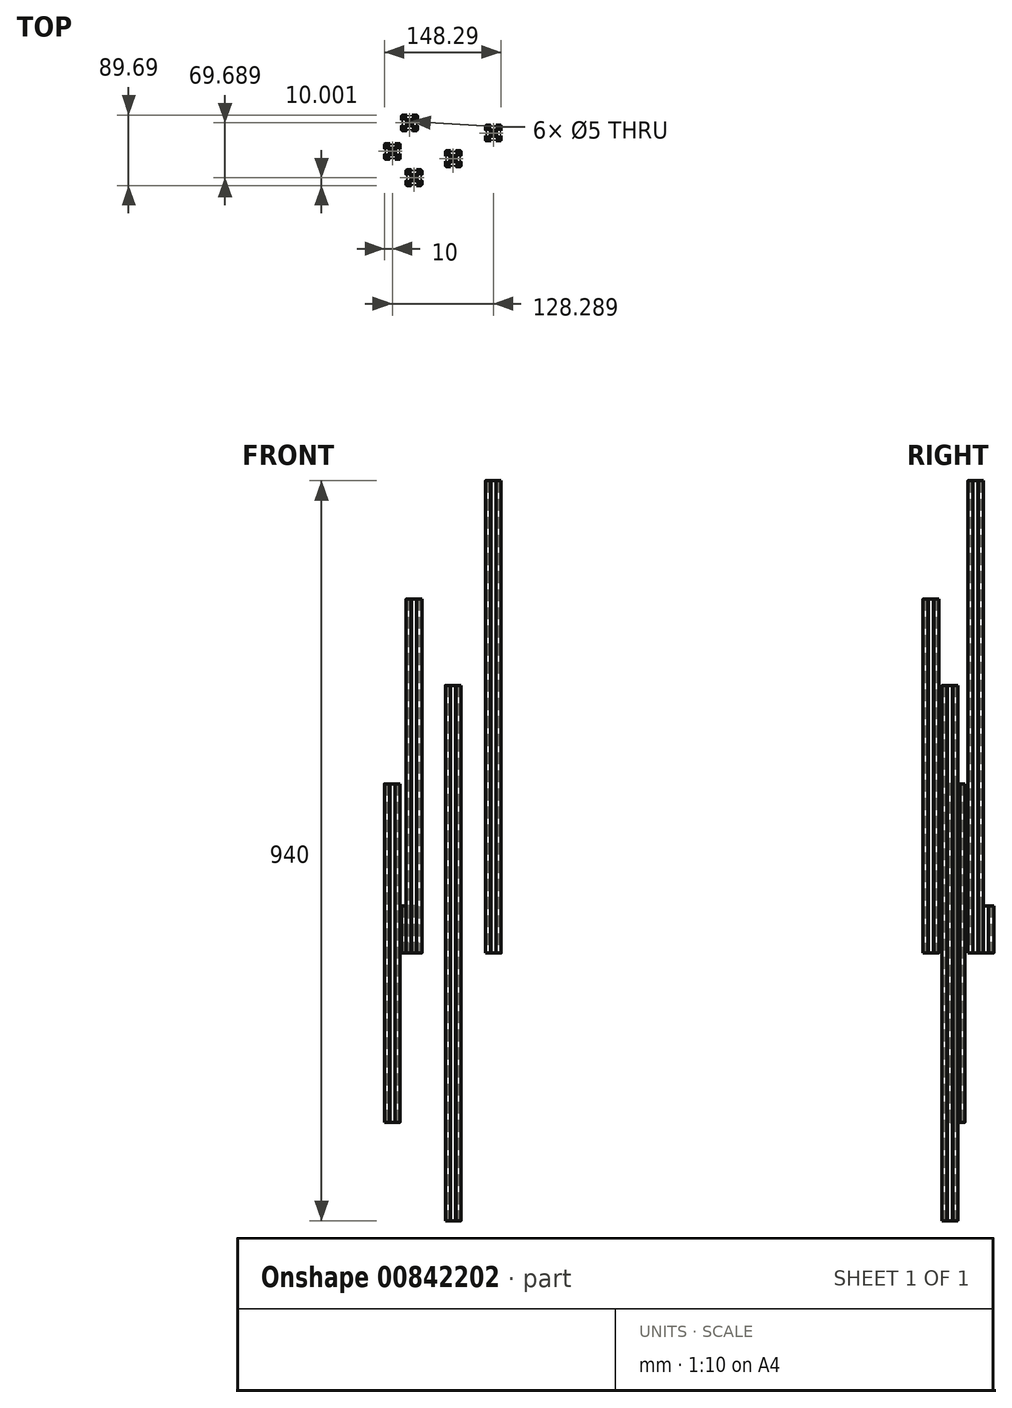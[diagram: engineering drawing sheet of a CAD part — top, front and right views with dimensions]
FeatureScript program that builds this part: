
annotation { "Feature Type Name" : "Feature", "Feature Type Description" : "" }
export const myFeature = defineFeature(function(context is Context, id is Id, definition is map)
    precondition{}
    {
        {
            var Q0;
            Q0=qCreatedBy(makeId("Top.planeOp"),FACE);
            var sketch = newSketch(context, id + "F0", { "sketchPlane" : qUnion([Q0])});
            skCircle(sketch, "E0", {"center": v(-10.22, 3.28) * mm, "radius": 2.5 * mm});
            skLineSegment(sketch, "E1.bottom", {"start": v(-1.72, -6.72) * mm, "end": v(-6.12, -6.72) * mm});
            skLineSegment(sketch, "E1.top", {"start": v(-1.72, 13.28) * mm, "end": v(-6.12, 13.28) * mm});
            skLineSegment(sketch, "E1.left", {"start": v(-0.22, -5.22) * mm, "end": v(-0.22, -0.32) * mm});
            skLineSegment(sketch, "E2.bottom", {"start": v(-8.21, -0.62) * mm, "end": v(-12.24, -0.62) * mm});
            skLineSegment(sketch, "E2.top", {"start": v(-8.21, 7.18) * mm, "end": v(-12.24, 7.18) * mm});
            skLineSegment(sketch, "E2.left", {"start": v(-6.32, 1.27) * mm, "end": v(-6.32, 5.3) * mm});
            skLineSegment(sketch, "E2.right", {"start": v(-14.12, 1.27) * mm, "end": v(-14.12, 5.3) * mm});
            skLineSegment(sketch, "E3.bottom", {"start": v(-1.72, 13.28) * mm, "end": v(-4.72, 13.28) * mm});
            skLineSegment(sketch, "E3.left", {"start": v(-0.22, 11.78) * mm, "end": v(-0.22, 8.78) * mm});
            skLineSegment(sketch, "E3.right", {"start": v(-4.72, 11.48) * mm, "end": v(-4.72, 9.84) * mm});
            skLineSegment(sketch, "E4", {"start": v(-5.74, 6.7) * mm, "end": v(-3.66, 8.78) * mm});
            skLineSegment(sketch, "E5.MirrorCS", {"start": v(-6.8, 7.77) * mm, "end": v(-4.72, 9.84) * mm});
            skLineSegment(sketch, "E6", {"start": v(-2.02, 8.78) * mm, "end": v(-2.02, 6.38) * mm});
            skLineSegment(sketch, "E7", {"start": v(-0.52, 6.88) * mm, "end": v(-0.22, 6.88) * mm});
            skLineSegment(sketch, "E8", {"start": v(-2.02, 6.38) * mm, "end": v(-0.72, 6.38) * mm});
            skLineSegment(sketch, "E9", {"start": v(-0.72, 6.68) * mm, "end": v(-0.72, 6.38) * mm});
            skPoint(sketch, "E10.visualSharp", {"position": v(-0.72, 6.88) * mm});
            skArc(sketch, "E10.filletArc", {"start": v(-0.52, 6.88) * mm, "mid": v(-0.67, 6.82) * mm, "end": v(-0.72, 6.68) * mm});
            skPoint(sketch, "E11.newPointA", {"position": v(-6.32, 6.12) * mm});
            skArc(sketch, "E11.filletArc", {"start": v(-5.74, 6.7) * mm, "mid": v(-6.17, 6.06) * mm, "end": v(-6.32, 5.3) * mm});
            skPoint(sketch, "E12.newPointA", {"position": v(-7.39, 7.18) * mm});
            skPoint(sketch, "E12.newPointB", {"position": v(-6.32, 7.18) * mm});
            skArc(sketch, "E12.filletArc", {"start": v(-8.21, 7.18) * mm, "mid": v(-7.45, 7.33) * mm, "end": v(-6.8, 7.77) * mm});
            skLineSegment(sketch, "E13.MirrorCS", {"start": v(-4.72, 11.48) * mm, "end": v(-7.12, 11.48) * mm});
            skLineSegment(sketch, "E14.MirrorCS", {"start": v(-7.12, 11.48) * mm, "end": v(-7.12, 12.78) * mm});
            skPoint(sketch, "E15.visualSharp", {"position": v(-0.22, 13.28) * mm});
            skArc(sketch, "E15.filletArc", {"start": v(-0.22, 11.78) * mm, "mid": v(-0.66, 12.84) * mm, "end": v(-1.72, 13.28) * mm});
            skLineSegment(sketch, "E16.trimOffspring", {"start": v(-2.02, 8.78) * mm, "end": v(-3.66, 8.78) * mm});
            skLineSegment(sketch, "E17.MirrorCS", {"start": v(-0.52, -0.32) * mm, "end": v(-0.22, -0.32) * mm});
            skArc(sketch, "E18.MirrorCS", {"start": v(-0.52, -0.32) * mm, "mid": v(-0.67, -0.26) * mm, "end": v(-0.72, -0.12) * mm});
            skLineSegment(sketch, "E19.MirrorCS", {"start": v(-0.72, -0.12) * mm, "end": v(-0.72, 0.18) * mm});
            skArc(sketch, "E20.MirrorCS", {"start": v(-5.74, -0.14) * mm, "mid": v(-6.17, 0.5) * mm, "end": v(-6.32, 1.27) * mm});
            skLineSegment(sketch, "E21.MirrorCS", {"start": v(-2.02, -2.22) * mm, "end": v(-3.66, -2.22) * mm});
            skLineSegment(sketch, "E22.MirrorCS", {"start": v(-2.02, 0.18) * mm, "end": v(-0.72, 0.18) * mm});
            skLineSegment(sketch, "E23.MirrorCS", {"start": v(-1.72, -6.72) * mm, "end": v(-4.72, -6.72) * mm});
            skPoint(sketch, "E24.MirrorP", {"position": v(-0.72, -0.32) * mm});
            skLineSegment(sketch, "E25.MirrorCS", {"start": v(-7.12, -4.92) * mm, "end": v(-7.12, -6.22) * mm});
            skLineSegment(sketch, "E26.MirrorCS", {"start": v(-4.72, -4.92) * mm, "end": v(-7.12, -4.92) * mm});
            skLineSegment(sketch, "E27.MirrorCS", {"start": v(-2.02, -2.22) * mm, "end": v(-2.02, 0.18) * mm});
            skLineSegment(sketch, "E28.MirrorCS", {"start": v(-0.22, -5.22) * mm, "end": v(-0.22, -2.22) * mm});
            skLineSegment(sketch, "E29.MirrorCS", {"start": v(-5.74, -0.14) * mm, "end": v(-3.66, -2.22) * mm});
            skPoint(sketch, "E30.MirrorP", {"position": v(-6.32, 0.44) * mm});
            skPoint(sketch, "E31.MirrorP", {"position": v(-0.22, -6.72) * mm});
            skPoint(sketch, "E32.MirrorP", {"position": v(-6.32, -0.62) * mm});
            skLineSegment(sketch, "E33.MirrorCS", {"start": v(-6.8, -1.2) * mm, "end": v(-4.72, -3.28) * mm});
            skPoint(sketch, "E34.MirrorP", {"position": v(-7.39, -0.62) * mm});
            skArc(sketch, "E35.MirrorCS", {"start": v(-0.22, -5.22) * mm, "mid": v(-0.66, -6.28) * mm, "end": v(-1.72, -6.72) * mm});
            skLineSegment(sketch, "E36.MirrorCS", {"start": v(-4.72, -4.92) * mm, "end": v(-4.72, -3.28) * mm});
            skArc(sketch, "E37.MirrorCS", {"start": v(-8.21, -0.62) * mm, "mid": v(-7.45, -0.77) * mm, "end": v(-6.8, -1.2) * mm});
            skLineSegment(sketch, "E38.trimOffspring", {"start": v(-0.22, 6.88) * mm, "end": v(-0.22, 11.78) * mm});
            skLineSegment(sketch, "E39.MirrorCS", {"start": v(-6.62, 12.98) * mm, "end": v(-6.62, 13.28) * mm});
            skArc(sketch, "E40.MirrorCS", {"start": v(-6.62, 12.98) * mm, "mid": v(-6.68, 12.84) * mm, "end": v(-6.82, 12.78) * mm});
            skLineSegment(sketch, "E41.MirrorCS", {"start": v(-6.82, 12.78) * mm, "end": v(-7.12, 12.78) * mm});
            skLineSegment(sketch, "E42", {"start": v(-6.12, 13.28) * mm, "end": v(-6.62, 13.28) * mm});
            skLineSegment(sketch, "E43.MirrorCS", {"start": v(-6.62, -6.42) * mm, "end": v(-6.62, -6.72) * mm});
            skLineSegment(sketch, "E44.MirrorCS", {"start": v(-6.82, -6.22) * mm, "end": v(-7.12, -6.22) * mm});
            skLineSegment(sketch, "E45.MirrorCS", {"start": v(-6.12, -6.72) * mm, "end": v(-6.62, -6.72) * mm});
            skArc(sketch, "E46.MirrorCS", {"start": v(-6.62, -6.42) * mm, "mid": v(-6.68, -6.28) * mm, "end": v(-6.82, -6.22) * mm});
            skArc(sketch, "E47.MirrorCS", {"start": v(-19.92, -0.32) * mm, "mid": v(-19.78, -0.26) * mm, "end": v(-19.72, -0.12) * mm});
            skLineSegment(sketch, "E48.MirrorCS", {"start": v(-19.92, 6.88) * mm, "end": v(-20.22, 6.88) * mm});
            skLineSegment(sketch, "E49.MirrorCS", {"start": v(-19.72, -0.12) * mm, "end": v(-19.72, 0.18) * mm});
            skArc(sketch, "E50.MirrorCS", {"start": v(-19.92, 6.88) * mm, "mid": v(-19.78, 6.82) * mm, "end": v(-19.72, 6.68) * mm});
            skLineSegment(sketch, "E51.MirrorCS", {"start": v(-19.72, 6.68) * mm, "end": v(-19.72, 6.38) * mm});
            skLineSegment(sketch, "E52.MirrorCS", {"start": v(-19.92, -0.32) * mm, "end": v(-20.22, -0.32) * mm});
            skLineSegment(sketch, "E53.MirrorCS", {"start": v(-14.32, 13.28) * mm, "end": v(-13.82, 13.28) * mm});
            skArc(sketch, "E54.MirrorCS", {"start": v(-20.22, -5.22) * mm, "mid": v(-19.79, -6.28) * mm, "end": v(-18.72, -6.72) * mm});
            skLineSegment(sketch, "E55.MirrorCS", {"start": v(-13.82, 12.98) * mm, "end": v(-13.82, 13.28) * mm});
            skArc(sketch, "E56.MirrorCS", {"start": v(-14.71, 6.7) * mm, "mid": v(-14.28, 6.06) * mm, "end": v(-14.12, 5.3) * mm});
            skLineSegment(sketch, "E57.MirrorCS", {"start": v(-13.62, -6.22) * mm, "end": v(-13.32, -6.22) * mm});
            skLineSegment(sketch, "E58.MirrorCS", {"start": v(-13.32, 11.48) * mm, "end": v(-13.32, 12.78) * mm});
            skLineSegment(sketch, "E59.MirrorCS", {"start": v(-12.24, 7.18) * mm, "end": v(-8.21, 7.18) * mm});
            skLineSegment(sketch, "E60.MirrorCS", {"start": v(-18.42, 0.18) * mm, "end": v(-19.72, 0.18) * mm});
            skLineSegment(sketch, "E61.MirrorCS", {"start": v(-18.42, 6.38) * mm, "end": v(-19.72, 6.38) * mm});
            skLineSegment(sketch, "E62.MirrorCS", {"start": v(-13.62, 12.78) * mm, "end": v(-13.32, 12.78) * mm});
            skArc(sketch, "E63.MirrorCS", {"start": v(-14.71, -0.14) * mm, "mid": v(-14.28, 0.5) * mm, "end": v(-14.12, 1.27) * mm});
            skArc(sketch, "E64.MirrorCS", {"start": v(-13.82, -6.42) * mm, "mid": v(-13.77, -6.28) * mm, "end": v(-13.62, -6.22) * mm});
            skArc(sketch, "E65.MirrorCS", {"start": v(-13.82, 12.98) * mm, "mid": v(-13.77, 12.84) * mm, "end": v(-13.62, 12.78) * mm});
            skLineSegment(sketch, "E66.MirrorCS", {"start": v(-13.82, -6.42) * mm, "end": v(-13.82, -6.72) * mm});
            skLineSegment(sketch, "E67.MirrorCS", {"start": v(-12.24, -0.62) * mm, "end": v(-8.21, -0.62) * mm});
            skLineSegment(sketch, "E68.MirrorCS", {"start": v(-14.32, -6.72) * mm, "end": v(-13.82, -6.72) * mm});
            skLineSegment(sketch, "E69.MirrorCS", {"start": v(-13.32, -4.92) * mm, "end": v(-13.32, -6.22) * mm});
            skArc(sketch, "E70.MirrorCS", {"start": v(-12.24, 7.18) * mm, "mid": v(-13, 7.33) * mm, "end": v(-13.65, 7.77) * mm});
            skPoint(sketch, "E71.MirrorP", {"position": v(-20.22, -6.72) * mm});
            skLineSegment(sketch, "E72.MirrorCS", {"start": v(-18.72, -6.72) * mm, "end": v(-14.32, -6.72) * mm});
            skPoint(sketch, "E73.MirrorP", {"position": v(-14.12, -0.62) * mm});
            skLineSegment(sketch, "E74.MirrorCS", {"start": v(-18.72, 13.28) * mm, "end": v(-14.32, 13.28) * mm});
            skArc(sketch, "E75.MirrorCS", {"start": v(-12.24, -0.62) * mm, "mid": v(-13, -0.77) * mm, "end": v(-13.65, -1.2) * mm});
            skArc(sketch, "E76.MirrorCS", {"start": v(-20.22, 11.78) * mm, "mid": v(-19.79, 12.84) * mm, "end": v(-18.72, 13.28) * mm});
            skPoint(sketch, "E77.MirrorP", {"position": v(-14.12, 0.44) * mm});
            skLineSegment(sketch, "E78.MirrorCS", {"start": v(-15.72, 11.48) * mm, "end": v(-15.72, 9.84) * mm});
            skLineSegment(sketch, "E79.MirrorCS", {"start": v(-13.65, 7.77) * mm, "end": v(-15.72, 9.84) * mm});
            skPoint(sketch, "E80.MirrorP", {"position": v(-14.12, 6.12) * mm});
            skLineSegment(sketch, "E81.MirrorCS", {"start": v(-18.42, -2.22) * mm, "end": v(-18.42, 0.18) * mm});
            skLineSegment(sketch, "E82.MirrorCS", {"start": v(-14.71, -0.14) * mm, "end": v(-16.79, -2.22) * mm});
            skLineSegment(sketch, "E83.MirrorCS", {"start": v(-15.72, -4.92) * mm, "end": v(-13.32, -4.92) * mm});
            skLineSegment(sketch, "E84.MirrorCS", {"start": v(-18.42, -2.22) * mm, "end": v(-16.79, -2.22) * mm});
            skLineSegment(sketch, "E85.MirrorCS", {"start": v(-20.22, -5.22) * mm, "end": v(-20.22, -2.22) * mm});
            skLineSegment(sketch, "E86.MirrorCS", {"start": v(-18.72, 13.28) * mm, "end": v(-15.72, 13.28) * mm});
            skLineSegment(sketch, "E87.MirrorCS", {"start": v(-20.22, 6.88) * mm, "end": v(-20.22, 11.78) * mm});
            skLineSegment(sketch, "E88.MirrorCS", {"start": v(-15.72, 11.48) * mm, "end": v(-13.32, 11.48) * mm});
            skLineSegment(sketch, "E89.MirrorCS", {"start": v(-13.65, -1.2) * mm, "end": v(-15.72, -3.28) * mm});
            skPoint(sketch, "E90.MirrorP", {"position": v(-13.06, -0.62) * mm});
            skLineSegment(sketch, "E91.MirrorCS", {"start": v(-18.42, 8.78) * mm, "end": v(-18.42, 6.38) * mm});
            skLineSegment(sketch, "E92.MirrorCS", {"start": v(-20.22, 11.78) * mm, "end": v(-20.22, 8.78) * mm});
            skPoint(sketch, "E93.MirrorP", {"position": v(-19.72, -0.32) * mm});
            skPoint(sketch, "E94.MirrorP", {"position": v(-20.22, 13.28) * mm});
            skPoint(sketch, "E95.MirrorP", {"position": v(-19.72, 6.88) * mm});
            skLineSegment(sketch, "E96.MirrorCS", {"start": v(-14.71, 6.7) * mm, "end": v(-16.79, 8.78) * mm});
            skLineSegment(sketch, "E97.MirrorCS", {"start": v(-18.42, 8.78) * mm, "end": v(-16.79, 8.78) * mm});
            skLineSegment(sketch, "E98.MirrorCS", {"start": v(-20.22, -5.22) * mm, "end": v(-20.22, -0.32) * mm});
            skLineSegment(sketch, "E99.MirrorCS", {"start": v(-18.72, -6.72) * mm, "end": v(-15.72, -6.72) * mm});
            skPoint(sketch, "E100.MirrorP", {"position": v(-14.12, 7.18) * mm});
            skPoint(sketch, "E101.MirrorP", {"position": v(-13.06, 7.18) * mm});
            skLineSegment(sketch, "E102.MirrorCS", {"start": v(-15.72, -4.92) * mm, "end": v(-15.72, -3.28) * mm});
            skSolve(sketch);
        }
        {
            var Q0;
            Q0=makeQuery(id+"F0.imprint","IMPRINT",FACE,{"disambiguationData":[TD([[makeQuery(id+"F0.imprint","IMPRINT",EDGE,{"derivedFrom":sQuery(id+"F0.wireOp",EDGE,"E1.bottom")}),-1.0]])]});
            extrude(context, id + "F1", {"entities" : qUnion([Q0]), "endBound" : BoundingType.SYMMETRIC, "depth" : 680 * mm, "offsetDistance" : 25 * mm});
        }
        {
            var Q0;
            Q0=qCreatedBy(makeId("Top.planeOp"),FACE);
            var sketch = newSketch(context, id + "F2", { "sketchPlane" : qUnion([Q0])});
            skCircle(sketch, "E103", {"center": v(-87.46, 12.57) * mm, "radius": 2.5 * mm});
            skLineSegment(sketch, "E104.bottom", {"start": v(-78.96, 2.57) * mm, "end": v(-83.36, 2.57) * mm});
            skLineSegment(sketch, "E104.top", {"start": v(-78.96, 22.57) * mm, "end": v(-83.36, 22.57) * mm});
            skLineSegment(sketch, "E104.left", {"start": v(-77.46, 4.07) * mm, "end": v(-77.46, 8.97) * mm});
            skLineSegment(sketch, "E105.bottom", {"start": v(-85.45, 8.67) * mm, "end": v(-89.47, 8.67) * mm});
            skLineSegment(sketch, "E105.top", {"start": v(-85.45, 16.47) * mm, "end": v(-89.47, 16.47) * mm});
            skLineSegment(sketch, "E105.left", {"start": v(-83.56, 10.56) * mm, "end": v(-83.56, 14.58) * mm});
            skLineSegment(sketch, "E105.right", {"start": v(-91.36, 10.56) * mm, "end": v(-91.36, 14.58) * mm});
            skLineSegment(sketch, "E106.bottom", {"start": v(-78.96, 22.57) * mm, "end": v(-81.96, 22.57) * mm});
            skLineSegment(sketch, "E106.left", {"start": v(-77.46, 21.07) * mm, "end": v(-77.46, 18.07) * mm});
            skLineSegment(sketch, "E106.right", {"start": v(-81.96, 20.77) * mm, "end": v(-81.96, 19.13) * mm});
            skLineSegment(sketch, "E107", {"start": v(-82.97, 16) * mm, "end": v(-80.9, 18.07) * mm});
            skLineSegment(sketch, "E108.MirrorCS", {"start": v(-84.04, 17.06) * mm, "end": v(-81.96, 19.13) * mm});
            skLineSegment(sketch, "E109", {"start": v(-79.26, 18.07) * mm, "end": v(-79.26, 15.67) * mm});
            skLineSegment(sketch, "E110", {"start": v(-77.76, 16.17) * mm, "end": v(-77.46, 16.17) * mm});
            skLineSegment(sketch, "E111", {"start": v(-79.26, 15.67) * mm, "end": v(-77.96, 15.67) * mm});
            skLineSegment(sketch, "E112", {"start": v(-77.96, 15.97) * mm, "end": v(-77.96, 15.67) * mm});
            skPoint(sketch, "E113.visualSharp", {"position": v(-77.96, 16.17) * mm});
            skArc(sketch, "E113.filletArc", {"start": v(-77.76, 16.17) * mm, "mid": v(-77.9, 16.11) * mm, "end": v(-77.96, 15.97) * mm});
            skPoint(sketch, "E114.newPointA", {"position": v(-83.56, 15.4) * mm});
            skArc(sketch, "E114.filletArc", {"start": v(-82.97, 16) * mm, "mid": v(-83.4, 15.35) * mm, "end": v(-83.56, 14.58) * mm});
            skPoint(sketch, "E115.newPointA", {"position": v(-84.62, 16.47) * mm});
            skPoint(sketch, "E115.newPointB", {"position": v(-83.56, 16.47) * mm});
            skArc(sketch, "E115.filletArc", {"start": v(-85.45, 16.47) * mm, "mid": v(-84.68, 16.62) * mm, "end": v(-84.04, 17.06) * mm});
            skLineSegment(sketch, "E116.MirrorCS", {"start": v(-81.96, 20.77) * mm, "end": v(-84.36, 20.77) * mm});
            skLineSegment(sketch, "E117.MirrorCS", {"start": v(-84.36, 20.77) * mm, "end": v(-84.36, 22.07) * mm});
            skPoint(sketch, "E118.visualSharp", {"position": v(-77.46, 22.57) * mm});
            skArc(sketch, "E118.filletArc", {"start": v(-77.46, 21.07) * mm, "mid": v(-77.9, 22.13) * mm, "end": v(-78.96, 22.57) * mm});
            skLineSegment(sketch, "E119.trimOffspring", {"start": v(-79.26, 18.07) * mm, "end": v(-80.9, 18.07) * mm});
            skLineSegment(sketch, "E120.MirrorCS", {"start": v(-77.76, 8.97) * mm, "end": v(-77.46, 8.97) * mm});
            skArc(sketch, "E121.MirrorCS", {"start": v(-77.76, 8.97) * mm, "mid": v(-77.9, 9.03) * mm, "end": v(-77.96, 9.17) * mm});
            skLineSegment(sketch, "E122.MirrorCS", {"start": v(-77.96, 9.17) * mm, "end": v(-77.96, 9.47) * mm});
            skArc(sketch, "E123.MirrorCS", {"start": v(-82.97, 9.15) * mm, "mid": v(-83.4, 9.8) * mm, "end": v(-83.56, 10.56) * mm});
            skLineSegment(sketch, "E124.MirrorCS", {"start": v(-79.26, 7.07) * mm, "end": v(-80.9, 7.07) * mm});
            skLineSegment(sketch, "E125.MirrorCS", {"start": v(-79.26, 9.47) * mm, "end": v(-77.96, 9.47) * mm});
            skLineSegment(sketch, "E126.MirrorCS", {"start": v(-78.96, 2.57) * mm, "end": v(-81.96, 2.57) * mm});
            skPoint(sketch, "E127.MirrorP", {"position": v(-77.96, 8.97) * mm});
            skLineSegment(sketch, "E128.MirrorCS", {"start": v(-84.36, 4.37) * mm, "end": v(-84.36, 3.07) * mm});
            skLineSegment(sketch, "E129.MirrorCS", {"start": v(-81.96, 4.37) * mm, "end": v(-84.36, 4.37) * mm});
            skLineSegment(sketch, "E130.MirrorCS", {"start": v(-79.26, 7.07) * mm, "end": v(-79.26, 9.47) * mm});
            skLineSegment(sketch, "E131.MirrorCS", {"start": v(-77.46, 4.07) * mm, "end": v(-77.46, 7.07) * mm});
            skLineSegment(sketch, "E132.MirrorCS", {"start": v(-82.97, 9.15) * mm, "end": v(-80.9, 7.07) * mm});
            skPoint(sketch, "E133.MirrorP", {"position": v(-83.56, 9.73) * mm});
            skPoint(sketch, "E134.MirrorP", {"position": v(-77.46, 2.57) * mm});
            skPoint(sketch, "E135.MirrorP", {"position": v(-83.56, 8.67) * mm});
            skLineSegment(sketch, "E136.MirrorCS", {"start": v(-84.04, 8.08) * mm, "end": v(-81.96, 6) * mm});
            skPoint(sketch, "E137.MirrorP", {"position": v(-84.62, 8.67) * mm});
            skArc(sketch, "E138.MirrorCS", {"start": v(-77.46, 4.07) * mm, "mid": v(-77.9, 3) * mm, "end": v(-78.96, 2.57) * mm});
            skLineSegment(sketch, "E139.MirrorCS", {"start": v(-81.96, 4.37) * mm, "end": v(-81.96, 6) * mm});
            skArc(sketch, "E140.MirrorCS", {"start": v(-85.45, 8.67) * mm, "mid": v(-84.68, 8.52) * mm, "end": v(-84.04, 8.08) * mm});
            skLineSegment(sketch, "E141.trimOffspring", {"start": v(-77.46, 16.17) * mm, "end": v(-77.46, 21.07) * mm});
            skLineSegment(sketch, "E142.MirrorCS", {"start": v(-83.86, 22.27) * mm, "end": v(-83.86, 22.57) * mm});
            skArc(sketch, "E143.MirrorCS", {"start": v(-83.86, 22.27) * mm, "mid": v(-83.92, 22.13) * mm, "end": v(-84.06, 22.07) * mm});
            skLineSegment(sketch, "E144.MirrorCS", {"start": v(-84.06, 22.07) * mm, "end": v(-84.36, 22.07) * mm});
            skLineSegment(sketch, "E145", {"start": v(-83.36, 22.57) * mm, "end": v(-83.86, 22.57) * mm});
            skLineSegment(sketch, "E146.MirrorCS", {"start": v(-83.86, 2.87) * mm, "end": v(-83.86, 2.57) * mm});
            skLineSegment(sketch, "E147.MirrorCS", {"start": v(-84.06, 3.07) * mm, "end": v(-84.36, 3.07) * mm});
            skLineSegment(sketch, "E148.MirrorCS", {"start": v(-83.36, 2.57) * mm, "end": v(-83.86, 2.57) * mm});
            skArc(sketch, "E149.MirrorCS", {"start": v(-83.86, 2.87) * mm, "mid": v(-83.92, 3.01) * mm, "end": v(-84.06, 3.07) * mm});
            skArc(sketch, "E150.MirrorCS", {"start": v(-97.16, 8.97) * mm, "mid": v(-97.02, 9.03) * mm, "end": v(-96.96, 9.17) * mm});
            skLineSegment(sketch, "E151.MirrorCS", {"start": v(-97.16, 16.17) * mm, "end": v(-97.46, 16.17) * mm});
            skLineSegment(sketch, "E152.MirrorCS", {"start": v(-96.96, 9.17) * mm, "end": v(-96.96, 9.47) * mm});
            skArc(sketch, "E153.MirrorCS", {"start": v(-97.16, 16.17) * mm, "mid": v(-97.02, 16.11) * mm, "end": v(-96.96, 15.97) * mm});
            skLineSegment(sketch, "E154.MirrorCS", {"start": v(-96.96, 15.97) * mm, "end": v(-96.96, 15.67) * mm});
            skLineSegment(sketch, "E155.MirrorCS", {"start": v(-97.16, 8.97) * mm, "end": v(-97.46, 8.97) * mm});
            skLineSegment(sketch, "E156.MirrorCS", {"start": v(-91.56, 22.57) * mm, "end": v(-91.06, 22.57) * mm});
            skArc(sketch, "E157.MirrorCS", {"start": v(-97.46, 4.07) * mm, "mid": v(-97.02, 3) * mm, "end": v(-95.96, 2.57) * mm});
            skLineSegment(sketch, "E158.MirrorCS", {"start": v(-91.06, 22.27) * mm, "end": v(-91.06, 22.57) * mm});
            skArc(sketch, "E159.MirrorCS", {"start": v(-91.95, 16) * mm, "mid": v(-91.51, 15.35) * mm, "end": v(-91.36, 14.58) * mm});
            skLineSegment(sketch, "E160.MirrorCS", {"start": v(-90.86, 3.07) * mm, "end": v(-90.56, 3.07) * mm});
            skLineSegment(sketch, "E161.MirrorCS", {"start": v(-90.56, 20.77) * mm, "end": v(-90.56, 22.07) * mm});
            skLineSegment(sketch, "E162.MirrorCS", {"start": v(-89.47, 16.47) * mm, "end": v(-85.45, 16.47) * mm});
            skLineSegment(sketch, "E163.MirrorCS", {"start": v(-95.66, 9.47) * mm, "end": v(-96.96, 9.47) * mm});
            skLineSegment(sketch, "E164.MirrorCS", {"start": v(-95.66, 15.67) * mm, "end": v(-96.96, 15.67) * mm});
            skLineSegment(sketch, "E165.MirrorCS", {"start": v(-90.86, 22.07) * mm, "end": v(-90.56, 22.07) * mm});
            skArc(sketch, "E166.MirrorCS", {"start": v(-91.95, 9.15) * mm, "mid": v(-91.51, 9.8) * mm, "end": v(-91.36, 10.56) * mm});
            skArc(sketch, "E167.MirrorCS", {"start": v(-91.06, 2.87) * mm, "mid": v(-91, 3.01) * mm, "end": v(-90.86, 3.07) * mm});
            skArc(sketch, "E168.MirrorCS", {"start": v(-91.06, 22.27) * mm, "mid": v(-91, 22.13) * mm, "end": v(-90.86, 22.07) * mm});
            skLineSegment(sketch, "E169.MirrorCS", {"start": v(-91.06, 2.87) * mm, "end": v(-91.06, 2.57) * mm});
            skLineSegment(sketch, "E170.MirrorCS", {"start": v(-89.47, 8.67) * mm, "end": v(-85.45, 8.67) * mm});
            skLineSegment(sketch, "E171.MirrorCS", {"start": v(-91.56, 2.57) * mm, "end": v(-91.06, 2.57) * mm});
            skLineSegment(sketch, "E172.MirrorCS", {"start": v(-90.56, 4.37) * mm, "end": v(-90.56, 3.07) * mm});
            skArc(sketch, "E173.MirrorCS", {"start": v(-89.47, 16.47) * mm, "mid": v(-90.24, 16.62) * mm, "end": v(-90.89, 17.06) * mm});
            skPoint(sketch, "E174.MirrorP", {"position": v(-97.46, 2.57) * mm});
            skLineSegment(sketch, "E175.MirrorCS", {"start": v(-95.96, 2.57) * mm, "end": v(-91.56, 2.57) * mm});
            skPoint(sketch, "E176.MirrorP", {"position": v(-91.36, 8.67) * mm});
            skLineSegment(sketch, "E177.MirrorCS", {"start": v(-95.96, 22.57) * mm, "end": v(-91.56, 22.57) * mm});
            skArc(sketch, "E178.MirrorCS", {"start": v(-89.47, 8.67) * mm, "mid": v(-90.24, 8.52) * mm, "end": v(-90.89, 8.08) * mm});
            skArc(sketch, "E179.MirrorCS", {"start": v(-97.46, 21.07) * mm, "mid": v(-97.02, 22.13) * mm, "end": v(-95.96, 22.57) * mm});
            skPoint(sketch, "E180.MirrorP", {"position": v(-91.36, 9.73) * mm});
            skLineSegment(sketch, "E181.MirrorCS", {"start": v(-92.96, 20.77) * mm, "end": v(-92.96, 19.13) * mm});
            skLineSegment(sketch, "E182.MirrorCS", {"start": v(-90.89, 17.06) * mm, "end": v(-92.96, 19.13) * mm});
            skPoint(sketch, "E183.MirrorP", {"position": v(-91.36, 15.4) * mm});
            skLineSegment(sketch, "E184.MirrorCS", {"start": v(-95.66, 7.07) * mm, "end": v(-95.66, 9.47) * mm});
            skLineSegment(sketch, "E185.MirrorCS", {"start": v(-91.95, 9.15) * mm, "end": v(-94.02, 7.07) * mm});
            skLineSegment(sketch, "E186.MirrorCS", {"start": v(-92.96, 4.37) * mm, "end": v(-90.56, 4.37) * mm});
            skLineSegment(sketch, "E187.MirrorCS", {"start": v(-95.66, 7.07) * mm, "end": v(-94.02, 7.07) * mm});
            skLineSegment(sketch, "E188.MirrorCS", {"start": v(-97.46, 4.07) * mm, "end": v(-97.46, 7.07) * mm});
            skLineSegment(sketch, "E189.MirrorCS", {"start": v(-95.96, 22.57) * mm, "end": v(-92.96, 22.57) * mm});
            skLineSegment(sketch, "E190.MirrorCS", {"start": v(-97.46, 16.17) * mm, "end": v(-97.46, 21.07) * mm});
            skLineSegment(sketch, "E191.MirrorCS", {"start": v(-92.96, 20.77) * mm, "end": v(-90.56, 20.77) * mm});
            skLineSegment(sketch, "E192.MirrorCS", {"start": v(-90.89, 8.08) * mm, "end": v(-92.96, 6) * mm});
            skPoint(sketch, "E193.MirrorP", {"position": v(-90.3, 8.67) * mm});
            skLineSegment(sketch, "E194.MirrorCS", {"start": v(-95.66, 18.07) * mm, "end": v(-95.66, 15.67) * mm});
            skLineSegment(sketch, "E195.MirrorCS", {"start": v(-97.46, 21.07) * mm, "end": v(-97.46, 18.07) * mm});
            skPoint(sketch, "E196.MirrorP", {"position": v(-96.96, 8.97) * mm});
            skPoint(sketch, "E197.MirrorP", {"position": v(-97.46, 22.57) * mm});
            skPoint(sketch, "E198.MirrorP", {"position": v(-96.96, 16.17) * mm});
            skLineSegment(sketch, "E199.MirrorCS", {"start": v(-91.95, 16) * mm, "end": v(-94.02, 18.07) * mm});
            skLineSegment(sketch, "E200.MirrorCS", {"start": v(-95.66, 18.07) * mm, "end": v(-94.02, 18.07) * mm});
            skLineSegment(sketch, "E201.MirrorCS", {"start": v(-97.46, 4.07) * mm, "end": v(-97.46, 8.97) * mm});
            skLineSegment(sketch, "E202.MirrorCS", {"start": v(-95.96, 2.57) * mm, "end": v(-92.96, 2.57) * mm});
            skPoint(sketch, "E203.MirrorP", {"position": v(-91.36, 16.47) * mm});
            skPoint(sketch, "E204.MirrorP", {"position": v(-90.3, 16.47) * mm});
            skLineSegment(sketch, "E205.MirrorCS", {"start": v(-92.96, 4.37) * mm, "end": v(-92.96, 6) * mm});
            skSolve(sketch);
        }
        {
            var Q0;
            Q0=makeQuery(id+"F2.imprint","IMPRINT",FACE,{"disambiguationData":[TD([[makeQuery(id+"F2.imprint","IMPRINT",EDGE,{"derivedFrom":sQuery(id+"F2.wireOp",EDGE,"E104.bottom")}),-1.0]])]});
            extrude(context, id + "F3", {"entities" : qUnion([Q0]), "endBound" : BoundingType.SYMMETRIC, "depth" : 430 * mm, "offsetDistance" : 25 * mm});
        }
        {
            var Q0;
            Q0=qCreatedBy(makeId("Top.planeOp"),FACE);
            var sketch = newSketch(context, id + "F4", { "sketchPlane" : qUnion([Q0])});
            skCircle(sketch, "E206", {"center": v(40.83, 35.88) * mm, "radius": 2.5 * mm});
            skLineSegment(sketch, "E207.bottom", {"start": v(49.33, 25.88) * mm, "end": v(44.93, 25.88) * mm});
            skLineSegment(sketch, "E207.top", {"start": v(49.33, 45.88) * mm, "end": v(44.93, 45.88) * mm});
            skLineSegment(sketch, "E207.left", {"start": v(50.83, 27.38) * mm, "end": v(50.83, 32.28) * mm});
            skLineSegment(sketch, "E208.bottom", {"start": v(42.84, 31.98) * mm, "end": v(38.82, 31.98) * mm});
            skLineSegment(sketch, "E208.top", {"start": v(42.84, 39.78) * mm, "end": v(38.82, 39.78) * mm});
            skLineSegment(sketch, "E208.left", {"start": v(44.73, 33.87) * mm, "end": v(44.73, 37.9) * mm});
            skLineSegment(sketch, "E208.right", {"start": v(36.93, 33.87) * mm, "end": v(36.93, 37.9) * mm});
            skLineSegment(sketch, "E209.bottom", {"start": v(49.33, 45.88) * mm, "end": v(46.33, 45.88) * mm});
            skLineSegment(sketch, "E209.left", {"start": v(50.83, 44.38) * mm, "end": v(50.83, 41.38) * mm});
            skLineSegment(sketch, "E209.right", {"start": v(46.33, 44.08) * mm, "end": v(46.33, 42.45) * mm});
            skLineSegment(sketch, "E210", {"start": v(45.31, 39.31) * mm, "end": v(47.39, 41.38) * mm});
            skLineSegment(sketch, "E211.MirrorCS", {"start": v(44.25, 40.37) * mm, "end": v(46.33, 42.45) * mm});
            skLineSegment(sketch, "E212", {"start": v(49.03, 41.38) * mm, "end": v(49.03, 38.98) * mm});
            skLineSegment(sketch, "E213", {"start": v(50.53, 39.48) * mm, "end": v(50.83, 39.48) * mm});
            skLineSegment(sketch, "E214", {"start": v(49.03, 38.98) * mm, "end": v(50.33, 38.98) * mm});
            skLineSegment(sketch, "E215", {"start": v(50.33, 39.28) * mm, "end": v(50.33, 38.98) * mm});
            skPoint(sketch, "E216.visualSharp", {"position": v(50.33, 39.48) * mm});
            skArc(sketch, "E216.filletArc", {"start": v(50.53, 39.48) * mm, "mid": v(50.39, 39.43) * mm, "end": v(50.33, 39.28) * mm});
            skPoint(sketch, "E217.newPointA", {"position": v(44.73, 38.72) * mm});
            skArc(sketch, "E217.filletArc", {"start": v(45.31, 39.31) * mm, "mid": v(44.88, 38.66) * mm, "end": v(44.73, 37.9) * mm});
            skPoint(sketch, "E218.newPointA", {"position": v(43.67, 39.78) * mm});
            skPoint(sketch, "E218.newPointB", {"position": v(44.73, 39.78) * mm});
            skArc(sketch, "E218.filletArc", {"start": v(42.84, 39.78) * mm, "mid": v(43.6, 39.94) * mm, "end": v(44.25, 40.37) * mm});
            skLineSegment(sketch, "E219.MirrorCS", {"start": v(46.33, 44.08) * mm, "end": v(43.93, 44.08) * mm});
            skLineSegment(sketch, "E220.MirrorCS", {"start": v(43.93, 44.08) * mm, "end": v(43.93, 45.38) * mm});
            skPoint(sketch, "E221.visualSharp", {"position": v(50.83, 45.88) * mm});
            skArc(sketch, "E221.filletArc", {"start": v(50.83, 44.38) * mm, "mid": v(50.39, 45.45) * mm, "end": v(49.33, 45.88) * mm});
            skLineSegment(sketch, "E222.trimOffspring", {"start": v(49.03, 41.38) * mm, "end": v(47.39, 41.38) * mm});
            skLineSegment(sketch, "E223.MirrorCS", {"start": v(50.53, 32.28) * mm, "end": v(50.83, 32.28) * mm});
            skArc(sketch, "E224.MirrorCS", {"start": v(50.53, 32.28) * mm, "mid": v(50.39, 32.34) * mm, "end": v(50.33, 32.48) * mm});
            skLineSegment(sketch, "E225.MirrorCS", {"start": v(50.33, 32.48) * mm, "end": v(50.33, 32.78) * mm});
            skArc(sketch, "E226.MirrorCS", {"start": v(45.31, 32.46) * mm, "mid": v(44.88, 33.1) * mm, "end": v(44.73, 33.87) * mm});
            skLineSegment(sketch, "E227.MirrorCS", {"start": v(49.03, 30.38) * mm, "end": v(47.39, 30.38) * mm});
            skLineSegment(sketch, "E228.MirrorCS", {"start": v(49.03, 32.78) * mm, "end": v(50.33, 32.78) * mm});
            skLineSegment(sketch, "E229.MirrorCS", {"start": v(49.33, 25.88) * mm, "end": v(46.33, 25.88) * mm});
            skPoint(sketch, "E230.MirrorP", {"position": v(50.33, 32.28) * mm});
            skLineSegment(sketch, "E231.MirrorCS", {"start": v(43.93, 27.68) * mm, "end": v(43.93, 26.38) * mm});
            skLineSegment(sketch, "E232.MirrorCS", {"start": v(46.33, 27.68) * mm, "end": v(43.93, 27.68) * mm});
            skLineSegment(sketch, "E233.MirrorCS", {"start": v(49.03, 30.38) * mm, "end": v(49.03, 32.78) * mm});
            skLineSegment(sketch, "E234.MirrorCS", {"start": v(50.83, 27.38) * mm, "end": v(50.83, 30.38) * mm});
            skLineSegment(sketch, "E235.MirrorCS", {"start": v(45.31, 32.46) * mm, "end": v(47.39, 30.38) * mm});
            skPoint(sketch, "E236.MirrorP", {"position": v(44.73, 33.05) * mm});
            skPoint(sketch, "E237.MirrorP", {"position": v(50.83, 25.88) * mm});
            skPoint(sketch, "E238.MirrorP", {"position": v(44.73, 31.98) * mm});
            skLineSegment(sketch, "E239.MirrorCS", {"start": v(44.25, 31.4) * mm, "end": v(46.33, 29.32) * mm});
            skPoint(sketch, "E240.MirrorP", {"position": v(43.67, 31.98) * mm});
            skArc(sketch, "E241.MirrorCS", {"start": v(50.83, 27.38) * mm, "mid": v(50.39, 26.32) * mm, "end": v(49.33, 25.88) * mm});
            skLineSegment(sketch, "E242.MirrorCS", {"start": v(46.33, 27.68) * mm, "end": v(46.33, 29.32) * mm});
            skArc(sketch, "E243.MirrorCS", {"start": v(42.84, 31.98) * mm, "mid": v(43.6, 31.83) * mm, "end": v(44.25, 31.4) * mm});
            skLineSegment(sketch, "E244.trimOffspring", {"start": v(50.83, 39.48) * mm, "end": v(50.83, 44.38) * mm});
            skLineSegment(sketch, "E245.MirrorCS", {"start": v(44.43, 45.58) * mm, "end": v(44.43, 45.88) * mm});
            skArc(sketch, "E246.MirrorCS", {"start": v(44.43, 45.58) * mm, "mid": v(44.37, 45.44) * mm, "end": v(44.23, 45.38) * mm});
            skLineSegment(sketch, "E247.MirrorCS", {"start": v(44.23, 45.38) * mm, "end": v(43.93, 45.38) * mm});
            skLineSegment(sketch, "E248", {"start": v(44.93, 45.88) * mm, "end": v(44.43, 45.88) * mm});
            skLineSegment(sketch, "E249.MirrorCS", {"start": v(44.43, 26.18) * mm, "end": v(44.43, 25.88) * mm});
            skLineSegment(sketch, "E250.MirrorCS", {"start": v(44.23, 26.38) * mm, "end": v(43.93, 26.38) * mm});
            skLineSegment(sketch, "E251.MirrorCS", {"start": v(44.93, 25.88) * mm, "end": v(44.43, 25.88) * mm});
            skArc(sketch, "E252.MirrorCS", {"start": v(44.43, 26.18) * mm, "mid": v(44.37, 26.33) * mm, "end": v(44.23, 26.38) * mm});
            skArc(sketch, "E253.MirrorCS", {"start": v(31.13, 32.28) * mm, "mid": v(31.27, 32.34) * mm, "end": v(31.33, 32.48) * mm});
            skLineSegment(sketch, "E254.MirrorCS", {"start": v(31.13, 39.48) * mm, "end": v(30.83, 39.48) * mm});
            skLineSegment(sketch, "E255.MirrorCS", {"start": v(31.33, 32.48) * mm, "end": v(31.33, 32.78) * mm});
            skArc(sketch, "E256.MirrorCS", {"start": v(31.13, 39.48) * mm, "mid": v(31.27, 39.43) * mm, "end": v(31.33, 39.28) * mm});
            skLineSegment(sketch, "E257.MirrorCS", {"start": v(31.33, 39.28) * mm, "end": v(31.33, 38.98) * mm});
            skLineSegment(sketch, "E258.MirrorCS", {"start": v(31.13, 32.28) * mm, "end": v(30.83, 32.28) * mm});
            skLineSegment(sketch, "E259.MirrorCS", {"start": v(36.73, 45.88) * mm, "end": v(37.23, 45.88) * mm});
            skArc(sketch, "E260.MirrorCS", {"start": v(30.83, 27.38) * mm, "mid": v(31.27, 26.32) * mm, "end": v(32.33, 25.88) * mm});
            skLineSegment(sketch, "E261.MirrorCS", {"start": v(37.23, 45.58) * mm, "end": v(37.23, 45.88) * mm});
            skArc(sketch, "E262.MirrorCS", {"start": v(36.34, 39.31) * mm, "mid": v(36.78, 38.66) * mm, "end": v(36.93, 37.9) * mm});
            skLineSegment(sketch, "E263.MirrorCS", {"start": v(37.43, 26.38) * mm, "end": v(37.73, 26.38) * mm});
            skLineSegment(sketch, "E264.MirrorCS", {"start": v(37.73, 44.08) * mm, "end": v(37.73, 45.38) * mm});
            skLineSegment(sketch, "E265.MirrorCS", {"start": v(38.82, 39.78) * mm, "end": v(42.84, 39.78) * mm});
            skLineSegment(sketch, "E266.MirrorCS", {"start": v(32.63, 32.78) * mm, "end": v(31.33, 32.78) * mm});
            skLineSegment(sketch, "E267.MirrorCS", {"start": v(32.63, 38.98) * mm, "end": v(31.33, 38.98) * mm});
            skLineSegment(sketch, "E268.MirrorCS", {"start": v(37.43, 45.38) * mm, "end": v(37.73, 45.38) * mm});
            skArc(sketch, "E269.MirrorCS", {"start": v(36.34, 32.46) * mm, "mid": v(36.78, 33.1) * mm, "end": v(36.93, 33.87) * mm});
            skArc(sketch, "E270.MirrorCS", {"start": v(37.23, 26.18) * mm, "mid": v(37.29, 26.33) * mm, "end": v(37.43, 26.38) * mm});
            skArc(sketch, "E271.MirrorCS", {"start": v(37.23, 45.58) * mm, "mid": v(37.29, 45.44) * mm, "end": v(37.43, 45.38) * mm});
            skLineSegment(sketch, "E272.MirrorCS", {"start": v(37.23, 26.18) * mm, "end": v(37.23, 25.88) * mm});
            skLineSegment(sketch, "E273.MirrorCS", {"start": v(38.82, 31.98) * mm, "end": v(42.84, 31.98) * mm});
            skLineSegment(sketch, "E274.MirrorCS", {"start": v(36.73, 25.88) * mm, "end": v(37.23, 25.88) * mm});
            skLineSegment(sketch, "E275.MirrorCS", {"start": v(37.73, 27.68) * mm, "end": v(37.73, 26.38) * mm});
            skArc(sketch, "E276.MirrorCS", {"start": v(38.82, 39.78) * mm, "mid": v(38.05, 39.94) * mm, "end": v(37.4, 40.37) * mm});
            skPoint(sketch, "E277.MirrorP", {"position": v(30.83, 25.88) * mm});
            skLineSegment(sketch, "E278.MirrorCS", {"start": v(32.33, 25.88) * mm, "end": v(36.73, 25.88) * mm});
            skPoint(sketch, "E279.MirrorP", {"position": v(36.93, 31.98) * mm});
            skLineSegment(sketch, "E280.MirrorCS", {"start": v(32.33, 45.88) * mm, "end": v(36.73, 45.88) * mm});
            skArc(sketch, "E281.MirrorCS", {"start": v(38.82, 31.98) * mm, "mid": v(38.05, 31.83) * mm, "end": v(37.4, 31.4) * mm});
            skArc(sketch, "E282.MirrorCS", {"start": v(30.83, 44.38) * mm, "mid": v(31.27, 45.45) * mm, "end": v(32.33, 45.88) * mm});
            skPoint(sketch, "E283.MirrorP", {"position": v(36.93, 33.05) * mm});
            skLineSegment(sketch, "E284.MirrorCS", {"start": v(35.33, 44.08) * mm, "end": v(35.33, 42.45) * mm});
            skLineSegment(sketch, "E285.MirrorCS", {"start": v(37.4, 40.37) * mm, "end": v(35.33, 42.45) * mm});
            skPoint(sketch, "E286.MirrorP", {"position": v(36.93, 38.72) * mm});
            skLineSegment(sketch, "E287.MirrorCS", {"start": v(32.63, 30.38) * mm, "end": v(32.63, 32.78) * mm});
            skLineSegment(sketch, "E288.MirrorCS", {"start": v(36.34, 32.46) * mm, "end": v(34.27, 30.38) * mm});
            skLineSegment(sketch, "E289.MirrorCS", {"start": v(35.33, 27.68) * mm, "end": v(37.73, 27.68) * mm});
            skLineSegment(sketch, "E290.MirrorCS", {"start": v(32.63, 30.38) * mm, "end": v(34.27, 30.38) * mm});
            skLineSegment(sketch, "E291.MirrorCS", {"start": v(30.83, 27.38) * mm, "end": v(30.83, 30.38) * mm});
            skLineSegment(sketch, "E292.MirrorCS", {"start": v(32.33, 45.88) * mm, "end": v(35.33, 45.88) * mm});
            skLineSegment(sketch, "E293.MirrorCS", {"start": v(30.83, 39.48) * mm, "end": v(30.83, 44.38) * mm});
            skLineSegment(sketch, "E294.MirrorCS", {"start": v(35.33, 44.08) * mm, "end": v(37.73, 44.08) * mm});
            skLineSegment(sketch, "E295.MirrorCS", {"start": v(37.4, 31.4) * mm, "end": v(35.33, 29.32) * mm});
            skPoint(sketch, "E296.MirrorP", {"position": v(37.99, 31.98) * mm});
            skLineSegment(sketch, "E297.MirrorCS", {"start": v(32.63, 41.38) * mm, "end": v(32.63, 38.98) * mm});
            skLineSegment(sketch, "E298.MirrorCS", {"start": v(30.83, 44.38) * mm, "end": v(30.83, 41.38) * mm});
            skPoint(sketch, "E299.MirrorP", {"position": v(31.33, 32.28) * mm});
            skPoint(sketch, "E300.MirrorP", {"position": v(30.83, 45.88) * mm});
            skPoint(sketch, "E301.MirrorP", {"position": v(31.33, 39.48) * mm});
            skLineSegment(sketch, "E302.MirrorCS", {"start": v(36.34, 39.31) * mm, "end": v(34.27, 41.38) * mm});
            skLineSegment(sketch, "E303.MirrorCS", {"start": v(32.63, 41.38) * mm, "end": v(34.27, 41.38) * mm});
            skLineSegment(sketch, "E304.MirrorCS", {"start": v(30.83, 27.38) * mm, "end": v(30.83, 32.28) * mm});
            skLineSegment(sketch, "E305.MirrorCS", {"start": v(32.33, 25.88) * mm, "end": v(35.33, 25.88) * mm});
            skPoint(sketch, "E306.MirrorP", {"position": v(36.93, 39.78) * mm});
            skPoint(sketch, "E307.MirrorP", {"position": v(37.99, 39.78) * mm});
            skLineSegment(sketch, "E308.MirrorCS", {"start": v(35.33, 27.68) * mm, "end": v(35.33, 29.32) * mm});
            skSolve(sketch);
        }
        {
            var Q0;
            Q0=makeQuery(id+"F4.imprint","IMPRINT",FACE,{"disambiguationData":[TD([[makeQuery(id+"F4.imprint","IMPRINT",EDGE,{"derivedFrom":sQuery(id+"F4.wireOp",EDGE,"E207.bottom")}),-1.0]])]});
            extrude(context, id + "F5", {"entities" : qUnion([Q0]), "depth" : 600 * mm, "offsetDistance" : 25 * mm});
        }
        {
            var Q0;
            Q0=qCreatedBy(makeId("Top.planeOp"),FACE);
            var sketch = newSketch(context, id + "F6", { "sketchPlane" : qUnion([Q0])});
            skCircle(sketch, "E309", {"center": v(-60.07, -20.8) * mm, "radius": 2.5 * mm});
            skLineSegment(sketch, "E310.bottom", {"start": v(-51.57, -30.8) * mm, "end": v(-55.97, -30.8) * mm});
            skLineSegment(sketch, "E310.top", {"start": v(-51.57, -10.8) * mm, "end": v(-55.97, -10.8) * mm});
            skLineSegment(sketch, "E310.left", {"start": v(-50.07, -29.3) * mm, "end": v(-50.07, -24.4) * mm});
            skLineSegment(sketch, "E311.bottom", {"start": v(-58.05, -24.7) * mm, "end": v(-62.08, -24.7) * mm});
            skLineSegment(sketch, "E311.top", {"start": v(-58.05, -16.9) * mm, "end": v(-62.08, -16.9) * mm});
            skLineSegment(sketch, "E311.left", {"start": v(-56.17, -22.82) * mm, "end": v(-56.17, -18.8) * mm});
            skLineSegment(sketch, "E311.right", {"start": v(-63.97, -22.82) * mm, "end": v(-63.97, -18.8) * mm});
            skLineSegment(sketch, "E312.bottom", {"start": v(-51.57, -10.8) * mm, "end": v(-54.57, -10.8) * mm});
            skLineSegment(sketch, "E312.left", {"start": v(-50.07, -12.3) * mm, "end": v(-50.07, -15.3) * mm});
            skLineSegment(sketch, "E312.right", {"start": v(-54.57, -12.6) * mm, "end": v(-54.57, -14.25) * mm});
            skLineSegment(sketch, "E313", {"start": v(-55.58, -17.38) * mm, "end": v(-53.5, -15.3) * mm});
            skLineSegment(sketch, "E314.MirrorCS", {"start": v(-56.64, -16.32) * mm, "end": v(-54.57, -14.25) * mm});
            skLineSegment(sketch, "E315", {"start": v(-51.87, -15.3) * mm, "end": v(-51.87, -17.7) * mm});
            skLineSegment(sketch, "E316", {"start": v(-50.37, -17.2) * mm, "end": v(-50.07, -17.2) * mm});
            skLineSegment(sketch, "E317", {"start": v(-51.87, -17.7) * mm, "end": v(-50.57, -17.7) * mm});
            skLineSegment(sketch, "E318", {"start": v(-50.57, -17.4) * mm, "end": v(-50.57, -17.7) * mm});
            skPoint(sketch, "E319.visualSharp", {"position": v(-50.57, -17.2) * mm});
            skArc(sketch, "E319.filletArc", {"start": v(-50.37, -17.2) * mm, "mid": v(-50.5, -17.27) * mm, "end": v(-50.57, -17.4) * mm});
            skPoint(sketch, "E320.newPointA", {"position": v(-56.17, -17.97) * mm});
            skArc(sketch, "E320.filletArc", {"start": v(-55.58, -17.38) * mm, "mid": v(-56.01, -18.03) * mm, "end": v(-56.17, -18.8) * mm});
            skPoint(sketch, "E321.newPointA", {"position": v(-57.23, -16.9) * mm});
            skPoint(sketch, "E321.newPointB", {"position": v(-56.17, -16.9) * mm});
            skArc(sketch, "E321.filletArc", {"start": v(-58.05, -16.9) * mm, "mid": v(-57.29, -16.76) * mm, "end": v(-56.64, -16.32) * mm});
            skLineSegment(sketch, "E322.MirrorCS", {"start": v(-54.57, -12.6) * mm, "end": v(-56.97, -12.6) * mm});
            skLineSegment(sketch, "E323.MirrorCS", {"start": v(-56.97, -12.6) * mm, "end": v(-56.97, -11.3) * mm});
            skPoint(sketch, "E324.visualSharp", {"position": v(-50.07, -10.8) * mm});
            skArc(sketch, "E324.filletArc", {"start": v(-50.07, -12.3) * mm, "mid": v(-50.5, -11.25) * mm, "end": v(-51.57, -10.8) * mm});
            skLineSegment(sketch, "E325.trimOffspring", {"start": v(-51.87, -15.3) * mm, "end": v(-53.5, -15.3) * mm});
            skLineSegment(sketch, "E326.MirrorCS", {"start": v(-50.37, -24.4) * mm, "end": v(-50.07, -24.4) * mm});
            skArc(sketch, "E327.MirrorCS", {"start": v(-50.37, -24.4) * mm, "mid": v(-50.5, -24.35) * mm, "end": v(-50.57, -24.2) * mm});
            skLineSegment(sketch, "E328.MirrorCS", {"start": v(-50.57, -24.2) * mm, "end": v(-50.57, -23.9) * mm});
            skArc(sketch, "E329.MirrorCS", {"start": v(-55.58, -24.23) * mm, "mid": v(-56.01, -23.59) * mm, "end": v(-56.17, -22.82) * mm});
            skLineSegment(sketch, "E330.MirrorCS", {"start": v(-51.87, -26.3) * mm, "end": v(-53.5, -26.3) * mm});
            skLineSegment(sketch, "E331.MirrorCS", {"start": v(-51.87, -23.9) * mm, "end": v(-50.57, -23.9) * mm});
            skLineSegment(sketch, "E332.MirrorCS", {"start": v(-51.57, -30.8) * mm, "end": v(-54.57, -30.8) * mm});
            skPoint(sketch, "E333.MirrorP", {"position": v(-50.57, -24.4) * mm});
            skLineSegment(sketch, "E334.MirrorCS", {"start": v(-56.97, -29) * mm, "end": v(-56.97, -30.3) * mm});
            skLineSegment(sketch, "E335.MirrorCS", {"start": v(-54.57, -29) * mm, "end": v(-56.97, -29) * mm});
            skLineSegment(sketch, "E336.MirrorCS", {"start": v(-51.87, -26.3) * mm, "end": v(-51.87, -23.9) * mm});
            skLineSegment(sketch, "E337.MirrorCS", {"start": v(-50.07, -29.3) * mm, "end": v(-50.07, -26.3) * mm});
            skLineSegment(sketch, "E338.MirrorCS", {"start": v(-55.58, -24.23) * mm, "end": v(-53.5, -26.3) * mm});
            skPoint(sketch, "E339.MirrorP", {"position": v(-56.17, -23.65) * mm});
            skPoint(sketch, "E340.MirrorP", {"position": v(-50.07, -30.8) * mm});
            skPoint(sketch, "E341.MirrorP", {"position": v(-56.17, -24.7) * mm});
            skLineSegment(sketch, "E342.MirrorCS", {"start": v(-56.64, -25.3) * mm, "end": v(-54.57, -27.37) * mm});
            skPoint(sketch, "E343.MirrorP", {"position": v(-57.23, -24.7) * mm});
            skArc(sketch, "E344.MirrorCS", {"start": v(-50.07, -29.3) * mm, "mid": v(-50.5, -30.37) * mm, "end": v(-51.57, -30.8) * mm});
            skLineSegment(sketch, "E345.MirrorCS", {"start": v(-54.57, -29) * mm, "end": v(-54.57, -27.37) * mm});
            skArc(sketch, "E346.MirrorCS", {"start": v(-58.05, -24.7) * mm, "mid": v(-57.29, -24.86) * mm, "end": v(-56.64, -25.3) * mm});
            skLineSegment(sketch, "E347.trimOffspring", {"start": v(-50.07, -17.2) * mm, "end": v(-50.07, -12.3) * mm});
            skLineSegment(sketch, "E348.MirrorCS", {"start": v(-56.47, -11.1) * mm, "end": v(-56.47, -10.8) * mm});
            skArc(sketch, "E349.MirrorCS", {"start": v(-56.47, -11.1) * mm, "mid": v(-56.52, -11.25) * mm, "end": v(-56.67, -11.3) * mm});
            skLineSegment(sketch, "E350.MirrorCS", {"start": v(-56.67, -11.3) * mm, "end": v(-56.97, -11.3) * mm});
            skLineSegment(sketch, "E351", {"start": v(-55.97, -10.8) * mm, "end": v(-56.47, -10.8) * mm});
            skLineSegment(sketch, "E352.MirrorCS", {"start": v(-56.47, -30.5) * mm, "end": v(-56.47, -30.8) * mm});
            skLineSegment(sketch, "E353.MirrorCS", {"start": v(-56.67, -30.3) * mm, "end": v(-56.97, -30.3) * mm});
            skLineSegment(sketch, "E354.MirrorCS", {"start": v(-55.97, -30.8) * mm, "end": v(-56.47, -30.8) * mm});
            skArc(sketch, "E355.MirrorCS", {"start": v(-56.47, -30.5) * mm, "mid": v(-56.52, -30.37) * mm, "end": v(-56.67, -30.3) * mm});
            skArc(sketch, "E356.MirrorCS", {"start": v(-69.77, -24.4) * mm, "mid": v(-69.62, -24.35) * mm, "end": v(-69.57, -24.2) * mm});
            skLineSegment(sketch, "E357.MirrorCS", {"start": v(-69.77, -17.2) * mm, "end": v(-70.07, -17.2) * mm});
            skLineSegment(sketch, "E358.MirrorCS", {"start": v(-69.57, -24.2) * mm, "end": v(-69.57, -23.9) * mm});
            skArc(sketch, "E359.MirrorCS", {"start": v(-69.77, -17.2) * mm, "mid": v(-69.62, -17.27) * mm, "end": v(-69.57, -17.4) * mm});
            skLineSegment(sketch, "E360.MirrorCS", {"start": v(-69.57, -17.4) * mm, "end": v(-69.57, -17.7) * mm});
            skLineSegment(sketch, "E361.MirrorCS", {"start": v(-69.77, -24.4) * mm, "end": v(-70.07, -24.4) * mm});
            skLineSegment(sketch, "E362.MirrorCS", {"start": v(-64.17, -10.8) * mm, "end": v(-63.67, -10.8) * mm});
            skArc(sketch, "E363.MirrorCS", {"start": v(-70.07, -29.3) * mm, "mid": v(-69.63, -30.37) * mm, "end": v(-68.57, -30.8) * mm});
            skLineSegment(sketch, "E364.MirrorCS", {"start": v(-63.67, -11.1) * mm, "end": v(-63.67, -10.8) * mm});
            skArc(sketch, "E365.MirrorCS", {"start": v(-64.55, -17.38) * mm, "mid": v(-64.12, -18.03) * mm, "end": v(-63.97, -18.8) * mm});
            skLineSegment(sketch, "E366.MirrorCS", {"start": v(-63.47, -30.3) * mm, "end": v(-63.17, -30.3) * mm});
            skLineSegment(sketch, "E367.MirrorCS", {"start": v(-63.17, -12.6) * mm, "end": v(-63.17, -11.3) * mm});
            skLineSegment(sketch, "E368.MirrorCS", {"start": v(-62.08, -16.9) * mm, "end": v(-58.05, -16.9) * mm});
            skLineSegment(sketch, "E369.MirrorCS", {"start": v(-68.27, -23.9) * mm, "end": v(-69.57, -23.9) * mm});
            skLineSegment(sketch, "E370.MirrorCS", {"start": v(-68.27, -17.7) * mm, "end": v(-69.57, -17.7) * mm});
            skLineSegment(sketch, "E371.MirrorCS", {"start": v(-63.47, -11.3) * mm, "end": v(-63.17, -11.3) * mm});
            skArc(sketch, "E372.MirrorCS", {"start": v(-64.55, -24.23) * mm, "mid": v(-64.12, -23.59) * mm, "end": v(-63.97, -22.82) * mm});
            skArc(sketch, "E373.MirrorCS", {"start": v(-63.67, -30.5) * mm, "mid": v(-63.6, -30.37) * mm, "end": v(-63.47, -30.3) * mm});
            skArc(sketch, "E374.MirrorCS", {"start": v(-63.67, -11.1) * mm, "mid": v(-63.6, -11.25) * mm, "end": v(-63.47, -11.3) * mm});
            skLineSegment(sketch, "E375.MirrorCS", {"start": v(-63.67, -30.5) * mm, "end": v(-63.67, -30.8) * mm});
            skLineSegment(sketch, "E376.MirrorCS", {"start": v(-62.08, -24.7) * mm, "end": v(-58.05, -24.7) * mm});
            skLineSegment(sketch, "E377.MirrorCS", {"start": v(-64.17, -30.8) * mm, "end": v(-63.67, -30.8) * mm});
            skLineSegment(sketch, "E378.MirrorCS", {"start": v(-63.17, -29) * mm, "end": v(-63.17, -30.3) * mm});
            skArc(sketch, "E379.MirrorCS", {"start": v(-62.08, -16.9) * mm, "mid": v(-62.84, -16.76) * mm, "end": v(-63.5, -16.32) * mm});
            skPoint(sketch, "E380.MirrorP", {"position": v(-70.07, -30.8) * mm});
            skLineSegment(sketch, "E381.MirrorCS", {"start": v(-68.57, -30.8) * mm, "end": v(-64.17, -30.8) * mm});
            skPoint(sketch, "E382.MirrorP", {"position": v(-63.97, -24.7) * mm});
            skLineSegment(sketch, "E383.MirrorCS", {"start": v(-68.57, -10.8) * mm, "end": v(-64.17, -10.8) * mm});
            skArc(sketch, "E384.MirrorCS", {"start": v(-62.08, -24.7) * mm, "mid": v(-62.84, -24.86) * mm, "end": v(-63.5, -25.3) * mm});
            skArc(sketch, "E385.MirrorCS", {"start": v(-70.07, -12.3) * mm, "mid": v(-69.63, -11.25) * mm, "end": v(-68.57, -10.8) * mm});
            skPoint(sketch, "E386.MirrorP", {"position": v(-63.97, -23.65) * mm});
            skLineSegment(sketch, "E387.MirrorCS", {"start": v(-65.57, -12.6) * mm, "end": v(-65.57, -14.25) * mm});
            skLineSegment(sketch, "E388.MirrorCS", {"start": v(-63.5, -16.32) * mm, "end": v(-65.57, -14.25) * mm});
            skPoint(sketch, "E389.MirrorP", {"position": v(-63.97, -17.97) * mm});
            skLineSegment(sketch, "E390.MirrorCS", {"start": v(-68.27, -26.3) * mm, "end": v(-68.27, -23.9) * mm});
            skLineSegment(sketch, "E391.MirrorCS", {"start": v(-64.55, -24.23) * mm, "end": v(-66.63, -26.3) * mm});
            skLineSegment(sketch, "E392.MirrorCS", {"start": v(-65.57, -29) * mm, "end": v(-63.17, -29) * mm});
            skLineSegment(sketch, "E393.MirrorCS", {"start": v(-68.27, -26.3) * mm, "end": v(-66.63, -26.3) * mm});
            skLineSegment(sketch, "E394.MirrorCS", {"start": v(-70.07, -29.3) * mm, "end": v(-70.07, -26.3) * mm});
            skLineSegment(sketch, "E395.MirrorCS", {"start": v(-68.57, -10.8) * mm, "end": v(-65.57, -10.8) * mm});
            skLineSegment(sketch, "E396.MirrorCS", {"start": v(-70.07, -17.2) * mm, "end": v(-70.07, -12.3) * mm});
            skLineSegment(sketch, "E397.MirrorCS", {"start": v(-65.57, -12.6) * mm, "end": v(-63.17, -12.6) * mm});
            skLineSegment(sketch, "E398.MirrorCS", {"start": v(-63.5, -25.3) * mm, "end": v(-65.57, -27.37) * mm});
            skPoint(sketch, "E399.MirrorP", {"position": v(-62.9, -24.7) * mm});
            skLineSegment(sketch, "E400.MirrorCS", {"start": v(-68.27, -15.3) * mm, "end": v(-68.27, -17.7) * mm});
            skLineSegment(sketch, "E401.MirrorCS", {"start": v(-70.07, -12.3) * mm, "end": v(-70.07, -15.3) * mm});
            skPoint(sketch, "E402.MirrorP", {"position": v(-69.57, -24.4) * mm});
            skPoint(sketch, "E403.MirrorP", {"position": v(-70.07, -10.8) * mm});
            skPoint(sketch, "E404.MirrorP", {"position": v(-69.57, -17.2) * mm});
            skLineSegment(sketch, "E405.MirrorCS", {"start": v(-64.55, -17.38) * mm, "end": v(-66.63, -15.3) * mm});
            skLineSegment(sketch, "E406.MirrorCS", {"start": v(-68.27, -15.3) * mm, "end": v(-66.63, -15.3) * mm});
            skLineSegment(sketch, "E407.MirrorCS", {"start": v(-70.07, -29.3) * mm, "end": v(-70.07, -24.4) * mm});
            skLineSegment(sketch, "E408.MirrorCS", {"start": v(-68.57, -30.8) * mm, "end": v(-65.57, -30.8) * mm});
            skPoint(sketch, "E409.MirrorP", {"position": v(-63.97, -16.9) * mm});
            skPoint(sketch, "E410.MirrorP", {"position": v(-62.9, -16.9) * mm});
            skLineSegment(sketch, "E411.MirrorCS", {"start": v(-65.57, -29) * mm, "end": v(-65.57, -27.37) * mm});
            skSolve(sketch);
        }
        {
            var Q0;
            Q0=makeQuery(id+"F6.imprint","IMPRINT",FACE,{"disambiguationData":[TD([[makeQuery(id+"F6.imprint","IMPRINT",EDGE,{"derivedFrom":sQuery(id+"F6.wireOp",EDGE,"E310.bottom")}),-1.0]])]});
            extrude(context, id + "F7", {"entities" : qUnion([Q0]), "depth" : 450 * mm, "offsetDistance" : 25 * mm});
        }
        {
            var Q0;
            Q0=qCreatedBy(makeId("Top.planeOp"),FACE);
            var sketch = newSketch(context, id + "F8", { "sketchPlane" : qUnion([Q0])});
            skCircle(sketch, "E412", {"center": v(-65.76, 48.88) * mm, "radius": 2.5 * mm});
            skLineSegment(sketch, "E413.bottom", {"start": v(-57.26, 38.88) * mm, "end": v(-61.66, 38.88) * mm});
            skLineSegment(sketch, "E413.top", {"start": v(-57.26, 58.88) * mm, "end": v(-61.66, 58.88) * mm});
            skLineSegment(sketch, "E413.left", {"start": v(-55.76, 40.38) * mm, "end": v(-55.76, 45.28) * mm});
            skLineSegment(sketch, "E414.bottom", {"start": v(-63.75, 44.98) * mm, "end": v(-67.77, 44.98) * mm});
            skLineSegment(sketch, "E414.top", {"start": v(-63.75, 52.78) * mm, "end": v(-67.77, 52.78) * mm});
            skLineSegment(sketch, "E414.left", {"start": v(-61.86, 46.87) * mm, "end": v(-61.86, 50.9) * mm});
            skLineSegment(sketch, "E414.right", {"start": v(-69.66, 46.87) * mm, "end": v(-69.66, 50.9) * mm});
            skLineSegment(sketch, "E415.bottom", {"start": v(-57.26, 58.88) * mm, "end": v(-60.26, 58.88) * mm});
            skLineSegment(sketch, "E415.left", {"start": v(-55.76, 57.38) * mm, "end": v(-55.76, 54.38) * mm});
            skLineSegment(sketch, "E415.right", {"start": v(-60.26, 57.08) * mm, "end": v(-60.26, 55.44) * mm});
            skLineSegment(sketch, "E416", {"start": v(-61.27, 52.3) * mm, "end": v(-59.2, 54.38) * mm});
            skLineSegment(sketch, "E417.MirrorCS", {"start": v(-62.33, 53.37) * mm, "end": v(-60.26, 55.44) * mm});
            skLineSegment(sketch, "E418", {"start": v(-57.56, 54.38) * mm, "end": v(-57.56, 51.98) * mm});
            skLineSegment(sketch, "E419", {"start": v(-56.06, 52.48) * mm, "end": v(-55.76, 52.48) * mm});
            skLineSegment(sketch, "E420", {"start": v(-57.56, 51.98) * mm, "end": v(-56.26, 51.98) * mm});
            skLineSegment(sketch, "E421", {"start": v(-56.26, 52.28) * mm, "end": v(-56.26, 51.98) * mm});
            skPoint(sketch, "E422.visualSharp", {"position": v(-56.26, 52.48) * mm});
            skArc(sketch, "E422.filletArc", {"start": v(-56.06, 52.48) * mm, "mid": v(-56.2, 52.42) * mm, "end": v(-56.26, 52.28) * mm});
            skPoint(sketch, "E423.newPointA", {"position": v(-61.86, 51.72) * mm});
            skArc(sketch, "E423.filletArc", {"start": v(-61.27, 52.3) * mm, "mid": v(-61.7, 51.66) * mm, "end": v(-61.86, 50.9) * mm});
            skPoint(sketch, "E424.newPointA", {"position": v(-62.92, 52.78) * mm});
            skPoint(sketch, "E424.newPointB", {"position": v(-61.86, 52.78) * mm});
            skArc(sketch, "E424.filletArc", {"start": v(-63.75, 52.78) * mm, "mid": v(-62.98, 52.93) * mm, "end": v(-62.33, 53.37) * mm});
            skLineSegment(sketch, "E425.MirrorCS", {"start": v(-60.26, 57.08) * mm, "end": v(-62.66, 57.08) * mm});
            skLineSegment(sketch, "E426.MirrorCS", {"start": v(-62.66, 57.08) * mm, "end": v(-62.66, 58.38) * mm});
            skPoint(sketch, "E427.visualSharp", {"position": v(-55.76, 58.88) * mm});
            skArc(sketch, "E427.filletArc", {"start": v(-55.76, 57.38) * mm, "mid": v(-56.2, 58.44) * mm, "end": v(-57.26, 58.88) * mm});
            skLineSegment(sketch, "E428.trimOffspring", {"start": v(-57.56, 54.38) * mm, "end": v(-59.2, 54.38) * mm});
            skLineSegment(sketch, "E429.MirrorCS", {"start": v(-56.06, 45.28) * mm, "end": v(-55.76, 45.28) * mm});
            skArc(sketch, "E430.MirrorCS", {"start": v(-56.06, 45.28) * mm, "mid": v(-56.2, 45.34) * mm, "end": v(-56.26, 45.48) * mm});
            skLineSegment(sketch, "E431.MirrorCS", {"start": v(-56.26, 45.48) * mm, "end": v(-56.26, 45.78) * mm});
            skArc(sketch, "E432.MirrorCS", {"start": v(-61.27, 45.45) * mm, "mid": v(-61.7, 46.1) * mm, "end": v(-61.86, 46.87) * mm});
            skLineSegment(sketch, "E433.MirrorCS", {"start": v(-57.56, 43.38) * mm, "end": v(-59.2, 43.38) * mm});
            skLineSegment(sketch, "E434.MirrorCS", {"start": v(-57.56, 45.78) * mm, "end": v(-56.26, 45.78) * mm});
            skLineSegment(sketch, "E435.MirrorCS", {"start": v(-57.26, 38.88) * mm, "end": v(-60.26, 38.88) * mm});
            skPoint(sketch, "E436.MirrorP", {"position": v(-56.26, 45.28) * mm});
            skLineSegment(sketch, "E437.MirrorCS", {"start": v(-62.66, 40.68) * mm, "end": v(-62.66, 39.38) * mm});
            skLineSegment(sketch, "E438.MirrorCS", {"start": v(-60.26, 40.68) * mm, "end": v(-62.66, 40.68) * mm});
            skLineSegment(sketch, "E439.MirrorCS", {"start": v(-57.56, 43.38) * mm, "end": v(-57.56, 45.78) * mm});
            skLineSegment(sketch, "E440.MirrorCS", {"start": v(-55.76, 40.38) * mm, "end": v(-55.76, 43.38) * mm});
            skLineSegment(sketch, "E441.MirrorCS", {"start": v(-61.27, 45.45) * mm, "end": v(-59.2, 43.38) * mm});
            skPoint(sketch, "E442.MirrorP", {"position": v(-61.86, 46.04) * mm});
            skPoint(sketch, "E443.MirrorP", {"position": v(-55.76, 38.88) * mm});
            skPoint(sketch, "E444.MirrorP", {"position": v(-61.86, 44.98) * mm});
            skLineSegment(sketch, "E445.MirrorCS", {"start": v(-62.33, 44.4) * mm, "end": v(-60.26, 42.32) * mm});
            skPoint(sketch, "E446.MirrorP", {"position": v(-62.92, 44.98) * mm});
            skArc(sketch, "E447.MirrorCS", {"start": v(-55.76, 40.38) * mm, "mid": v(-56.2, 39.32) * mm, "end": v(-57.26, 38.88) * mm});
            skLineSegment(sketch, "E448.MirrorCS", {"start": v(-60.26, 40.68) * mm, "end": v(-60.26, 42.32) * mm});
            skArc(sketch, "E449.MirrorCS", {"start": v(-63.75, 44.98) * mm, "mid": v(-62.98, 44.83) * mm, "end": v(-62.33, 44.4) * mm});
            skLineSegment(sketch, "E450.trimOffspring", {"start": v(-55.76, 52.48) * mm, "end": v(-55.76, 57.38) * mm});
            skLineSegment(sketch, "E451.MirrorCS", {"start": v(-62.16, 58.58) * mm, "end": v(-62.16, 58.88) * mm});
            skArc(sketch, "E452.MirrorCS", {"start": v(-62.16, 58.58) * mm, "mid": v(-62.22, 58.44) * mm, "end": v(-62.36, 58.38) * mm});
            skLineSegment(sketch, "E453.MirrorCS", {"start": v(-62.36, 58.38) * mm, "end": v(-62.66, 58.38) * mm});
            skLineSegment(sketch, "E454", {"start": v(-61.66, 58.88) * mm, "end": v(-62.16, 58.88) * mm});
            skLineSegment(sketch, "E455.MirrorCS", {"start": v(-62.16, 39.18) * mm, "end": v(-62.16, 38.88) * mm});
            skLineSegment(sketch, "E456.MirrorCS", {"start": v(-62.36, 39.38) * mm, "end": v(-62.66, 39.38) * mm});
            skLineSegment(sketch, "E457.MirrorCS", {"start": v(-61.66, 38.88) * mm, "end": v(-62.16, 38.88) * mm});
            skArc(sketch, "E458.MirrorCS", {"start": v(-62.16, 39.18) * mm, "mid": v(-62.22, 39.32) * mm, "end": v(-62.36, 39.38) * mm});
            skArc(sketch, "E459.MirrorCS", {"start": v(-75.46, 45.28) * mm, "mid": v(-75.32, 45.34) * mm, "end": v(-75.26, 45.48) * mm});
            skLineSegment(sketch, "E460.MirrorCS", {"start": v(-75.46, 52.48) * mm, "end": v(-75.76, 52.48) * mm});
            skLineSegment(sketch, "E461.MirrorCS", {"start": v(-75.26, 45.48) * mm, "end": v(-75.26, 45.78) * mm});
            skArc(sketch, "E462.MirrorCS", {"start": v(-75.46, 52.48) * mm, "mid": v(-75.32, 52.42) * mm, "end": v(-75.26, 52.28) * mm});
            skLineSegment(sketch, "E463.MirrorCS", {"start": v(-75.26, 52.28) * mm, "end": v(-75.26, 51.98) * mm});
            skLineSegment(sketch, "E464.MirrorCS", {"start": v(-75.46, 45.28) * mm, "end": v(-75.76, 45.28) * mm});
            skLineSegment(sketch, "E465.MirrorCS", {"start": v(-69.86, 58.88) * mm, "end": v(-69.36, 58.88) * mm});
            skArc(sketch, "E466.MirrorCS", {"start": v(-75.76, 40.38) * mm, "mid": v(-75.32, 39.32) * mm, "end": v(-74.26, 38.88) * mm});
            skLineSegment(sketch, "E467.MirrorCS", {"start": v(-69.36, 58.58) * mm, "end": v(-69.36, 58.88) * mm});
            skArc(sketch, "E468.MirrorCS", {"start": v(-70.24, 52.3) * mm, "mid": v(-69.81, 51.66) * mm, "end": v(-69.66, 50.9) * mm});
            skLineSegment(sketch, "E469.MirrorCS", {"start": v(-69.16, 39.38) * mm, "end": v(-68.86, 39.38) * mm});
            skLineSegment(sketch, "E470.MirrorCS", {"start": v(-68.86, 57.08) * mm, "end": v(-68.86, 58.38) * mm});
            skLineSegment(sketch, "E471.MirrorCS", {"start": v(-67.77, 52.78) * mm, "end": v(-63.75, 52.78) * mm});
            skLineSegment(sketch, "E472.MirrorCS", {"start": v(-73.96, 45.78) * mm, "end": v(-75.26, 45.78) * mm});
            skLineSegment(sketch, "E473.MirrorCS", {"start": v(-73.96, 51.98) * mm, "end": v(-75.26, 51.98) * mm});
            skLineSegment(sketch, "E474.MirrorCS", {"start": v(-69.16, 58.38) * mm, "end": v(-68.86, 58.38) * mm});
            skArc(sketch, "E475.MirrorCS", {"start": v(-70.24, 45.45) * mm, "mid": v(-69.81, 46.1) * mm, "end": v(-69.66, 46.87) * mm});
            skArc(sketch, "E476.MirrorCS", {"start": v(-69.36, 39.18) * mm, "mid": v(-69.3, 39.32) * mm, "end": v(-69.16, 39.38) * mm});
            skArc(sketch, "E477.MirrorCS", {"start": v(-69.36, 58.58) * mm, "mid": v(-69.3, 58.44) * mm, "end": v(-69.16, 58.38) * mm});
            skLineSegment(sketch, "E478.MirrorCS", {"start": v(-69.36, 39.18) * mm, "end": v(-69.36, 38.88) * mm});
            skLineSegment(sketch, "E479.MirrorCS", {"start": v(-67.77, 44.98) * mm, "end": v(-63.75, 44.98) * mm});
            skLineSegment(sketch, "E480.MirrorCS", {"start": v(-69.86, 38.88) * mm, "end": v(-69.36, 38.88) * mm});
            skLineSegment(sketch, "E481.MirrorCS", {"start": v(-68.86, 40.68) * mm, "end": v(-68.86, 39.38) * mm});
            skArc(sketch, "E482.MirrorCS", {"start": v(-67.77, 52.78) * mm, "mid": v(-68.54, 52.93) * mm, "end": v(-69.18, 53.37) * mm});
            skPoint(sketch, "E483.MirrorP", {"position": v(-75.76, 38.88) * mm});
            skLineSegment(sketch, "E484.MirrorCS", {"start": v(-74.26, 38.88) * mm, "end": v(-69.86, 38.88) * mm});
            skPoint(sketch, "E485.MirrorP", {"position": v(-69.66, 44.98) * mm});
            skLineSegment(sketch, "E486.MirrorCS", {"start": v(-74.26, 58.88) * mm, "end": v(-69.86, 58.88) * mm});
            skArc(sketch, "E487.MirrorCS", {"start": v(-67.77, 44.98) * mm, "mid": v(-68.54, 44.83) * mm, "end": v(-69.18, 44.4) * mm});
            skArc(sketch, "E488.MirrorCS", {"start": v(-75.76, 57.38) * mm, "mid": v(-75.32, 58.44) * mm, "end": v(-74.26, 58.88) * mm});
            skPoint(sketch, "E489.MirrorP", {"position": v(-69.66, 46.04) * mm});
            skLineSegment(sketch, "E490.MirrorCS", {"start": v(-71.26, 57.08) * mm, "end": v(-71.26, 55.44) * mm});
            skLineSegment(sketch, "E491.MirrorCS", {"start": v(-69.18, 53.37) * mm, "end": v(-71.26, 55.44) * mm});
            skPoint(sketch, "E492.MirrorP", {"position": v(-69.66, 51.72) * mm});
            skLineSegment(sketch, "E493.MirrorCS", {"start": v(-73.96, 43.38) * mm, "end": v(-73.96, 45.78) * mm});
            skLineSegment(sketch, "E494.MirrorCS", {"start": v(-70.24, 45.45) * mm, "end": v(-72.32, 43.38) * mm});
            skLineSegment(sketch, "E495.MirrorCS", {"start": v(-71.26, 40.68) * mm, "end": v(-68.86, 40.68) * mm});
            skLineSegment(sketch, "E496.MirrorCS", {"start": v(-73.96, 43.38) * mm, "end": v(-72.32, 43.38) * mm});
            skLineSegment(sketch, "E497.MirrorCS", {"start": v(-75.76, 40.38) * mm, "end": v(-75.76, 43.38) * mm});
            skLineSegment(sketch, "E498.MirrorCS", {"start": v(-74.26, 58.88) * mm, "end": v(-71.26, 58.88) * mm});
            skLineSegment(sketch, "E499.MirrorCS", {"start": v(-75.76, 52.48) * mm, "end": v(-75.76, 57.38) * mm});
            skLineSegment(sketch, "E500.MirrorCS", {"start": v(-71.26, 57.08) * mm, "end": v(-68.86, 57.08) * mm});
            skLineSegment(sketch, "E501.MirrorCS", {"start": v(-69.18, 44.4) * mm, "end": v(-71.26, 42.32) * mm});
            skPoint(sketch, "E502.MirrorP", {"position": v(-68.6, 44.98) * mm});
            skLineSegment(sketch, "E503.MirrorCS", {"start": v(-73.96, 54.38) * mm, "end": v(-73.96, 51.98) * mm});
            skLineSegment(sketch, "E504.MirrorCS", {"start": v(-75.76, 57.38) * mm, "end": v(-75.76, 54.38) * mm});
            skPoint(sketch, "E505.MirrorP", {"position": v(-75.26, 45.28) * mm});
            skPoint(sketch, "E506.MirrorP", {"position": v(-75.76, 58.88) * mm});
            skPoint(sketch, "E507.MirrorP", {"position": v(-75.26, 52.48) * mm});
            skLineSegment(sketch, "E508.MirrorCS", {"start": v(-70.24, 52.3) * mm, "end": v(-72.32, 54.38) * mm});
            skLineSegment(sketch, "E509.MirrorCS", {"start": v(-73.96, 54.38) * mm, "end": v(-72.32, 54.38) * mm});
            skLineSegment(sketch, "E510.MirrorCS", {"start": v(-75.76, 40.38) * mm, "end": v(-75.76, 45.28) * mm});
            skLineSegment(sketch, "E511.MirrorCS", {"start": v(-74.26, 38.88) * mm, "end": v(-71.26, 38.88) * mm});
            skPoint(sketch, "E512.MirrorP", {"position": v(-69.66, 52.78) * mm});
            skPoint(sketch, "E513.MirrorP", {"position": v(-68.6, 52.78) * mm});
            skLineSegment(sketch, "E514.MirrorCS", {"start": v(-71.26, 40.68) * mm, "end": v(-71.26, 42.32) * mm});
            skSolve(sketch);
        }
        {
            var Q0;
            Q0=makeQuery(id+"F8.imprint","IMPRINT",FACE,{"disambiguationData":[TD([[makeQuery(id+"F8.imprint","IMPRINT",EDGE,{"derivedFrom":sQuery(id+"F8.wireOp",EDGE,"E413.bottom")}),-1.0]])]});
            extrude(context, id + "F9", {"entities" : qUnion([Q0]), "depth" : 60 * mm, "offsetDistance" : 25 * mm});
        }
        {
            var Q0;
            Q0=makeQuery(id+"F1.opExtrude","SWEPT_BODY",BODY,{"disambiguationData":[OSD([sQuery(id+"F0.wireOp",EDGE,"E1.bottom"),sQuery(id+"F0.wireOp",EDGE,"E1.top"),sQuery(id+"F0.wireOp",EDGE,"E1.left"),sQuery(id+"F0.wireOp",EDGE,"E2.left"),sQuery(id+"F0.wireOp",EDGE,"E3.bottom"),sQuery(id+"F0.wireOp",EDGE,"E3.right"),sQuery(id+"F0.wireOp",EDGE,"E4"),sQuery(id+"F0.wireOp",EDGE,"E5.MirrorCS"),sQuery(id+"F0.wireOp",EDGE,"E6"),sQuery(id+"F0.wireOp",EDGE,"E7"),sQuery(id+"F0.wireOp",EDGE,"E8"),sQuery(id+"F0.wireOp",EDGE,"E9"),sQuery(id+"F0.wireOp",EDGE,"E10.filletArc"),sQuery(id+"F0.wireOp",EDGE,"E11.filletArc"),sQuery(id+"F0.wireOp",EDGE,"E12.filletArc"),sQuery(id+"F0.wireOp",EDGE,"E13.MirrorCS"),sQuery(id+"F0.wireOp",EDGE,"E14.MirrorCS"),sQuery(id+"F0.wireOp",EDGE,"E15.filletArc"),sQuery(id+"F0.wireOp",EDGE,"E16.trimOffspring"),sQuery(id+"F0.wireOp",EDGE,"E17.MirrorCS"),sQuery(id+"F0.wireOp",EDGE,"E18.MirrorCS"),sQuery(id+"F0.wireOp",EDGE,"E19.MirrorCS"),sQuery(id+"F0.wireOp",EDGE,"E20.MirrorCS"),sQuery(id+"F0.wireOp",EDGE,"E21.MirrorCS"),sQuery(id+"F0.wireOp",EDGE,"E22.MirrorCS"),sQuery(id+"F0.wireOp",EDGE,"E23.MirrorCS"),sQuery(id+"F0.wireOp",EDGE,"E25.MirrorCS"),sQuery(id+"F0.wireOp",EDGE,"E26.MirrorCS"),sQuery(id+"F0.wireOp",EDGE,"E27.MirrorCS"),sQuery(id+"F0.wireOp",EDGE,"E28.MirrorCS"),sQuery(id+"F0.wireOp",EDGE,"E29.MirrorCS"),sQuery(id+"F0.wireOp",EDGE,"E33.MirrorCS"),sQuery(id+"F0.wireOp",EDGE,"E35.MirrorCS"),sQuery(id+"F0.wireOp",EDGE,"E36.MirrorCS"),sQuery(id+"F0.wireOp",EDGE,"E37.MirrorCS"),sQuery(id+"F0.wireOp",EDGE,"E38.trimOffspring"),sQuery(id+"F0.wireOp",EDGE,"E39.MirrorCS"),sQuery(id+"F0.wireOp",EDGE,"E40.MirrorCS"),sQuery(id+"F0.wireOp",EDGE,"E41.MirrorCS"),sQuery(id+"F0.wireOp",EDGE,"E42"),sQuery(id+"F0.wireOp",EDGE,"E43.MirrorCS"),sQuery(id+"F0.wireOp",EDGE,"E44.MirrorCS"),sQuery(id+"F0.wireOp",EDGE,"E45.MirrorCS"),sQuery(id+"F0.wireOp",EDGE,"E46.MirrorCS"),sQuery(id+"F0.wireOp",EDGE,"E47.MirrorCS"),sQuery(id+"F0.wireOp",EDGE,"E48.MirrorCS"),sQuery(id+"F0.wireOp",EDGE,"E49.MirrorCS"),sQuery(id+"F0.wireOp",EDGE,"E50.MirrorCS"),sQuery(id+"F0.wireOp",EDGE,"E51.MirrorCS"),sQuery(id+"F0.wireOp",EDGE,"E52.MirrorCS"),sQuery(id+"F0.wireOp",EDGE,"E53.MirrorCS"),sQuery(id+"F0.wireOp",EDGE,"E54.MirrorCS"),sQuery(id+"F0.wireOp",EDGE,"E55.MirrorCS"),sQuery(id+"F0.wireOp",EDGE,"E56.MirrorCS"),sQuery(id+"F0.wireOp",EDGE,"E57.MirrorCS"),sQuery(id+"F0.wireOp",EDGE,"E58.MirrorCS"),sQuery(id+"F0.wireOp",EDGE,"E59.MirrorCS"),sQuery(id+"F0.wireOp",EDGE,"E60.MirrorCS"),sQuery(id+"F0.wireOp",EDGE,"E61.MirrorCS"),sQuery(id+"F0.wireOp",EDGE,"E62.MirrorCS"),sQuery(id+"F0.wireOp",EDGE,"E63.MirrorCS"),sQuery(id+"F0.wireOp",EDGE,"E64.MirrorCS"),sQuery(id+"F0.wireOp",EDGE,"E65.MirrorCS"),sQuery(id+"F0.wireOp",EDGE,"E66.MirrorCS"),sQuery(id+"F0.wireOp",EDGE,"E67.MirrorCS"),sQuery(id+"F0.wireOp",EDGE,"E68.MirrorCS"),sQuery(id+"F0.wireOp",EDGE,"E69.MirrorCS"),sQuery(id+"F0.wireOp",EDGE,"E70.MirrorCS"),sQuery(id+"F0.wireOp",EDGE,"E72.MirrorCS"),sQuery(id+"F0.wireOp",EDGE,"E74.MirrorCS"),sQuery(id+"F0.wireOp",EDGE,"E75.MirrorCS"),sQuery(id+"F0.wireOp",EDGE,"E76.MirrorCS"),sQuery(id+"F0.wireOp",EDGE,"E78.MirrorCS"),sQuery(id+"F0.wireOp",EDGE,"E79.MirrorCS"),sQuery(id+"F0.wireOp",EDGE,"E81.MirrorCS"),sQuery(id+"F0.wireOp",EDGE,"E82.MirrorCS"),sQuery(id+"F0.wireOp",EDGE,"E2.right"),sQuery(id+"F0.wireOp",EDGE,"E83.MirrorCS"),sQuery(id+"F0.wireOp",EDGE,"E84.MirrorCS"),sQuery(id+"F0.wireOp",EDGE,"E0"),sQuery(id+"F0.wireOp",EDGE,"E86.MirrorCS"),sQuery(id+"F0.wireOp",EDGE,"E87.MirrorCS"),sQuery(id+"F0.wireOp",EDGE,"E88.MirrorCS"),sQuery(id+"F0.wireOp",EDGE,"E89.MirrorCS"),sQuery(id+"F0.wireOp",EDGE,"E91.MirrorCS"),sQuery(id+"F0.wireOp",EDGE,"E92.MirrorCS"),sQuery(id+"F0.wireOp",EDGE,"E96.MirrorCS"),sQuery(id+"F0.wireOp",EDGE,"E97.MirrorCS"),sQuery(id+"F0.wireOp",EDGE,"E98.MirrorCS"),sQuery(id+"F0.wireOp",EDGE,"E99.MirrorCS"),sQuery(id+"F0.wireOp",EDGE,"E102.MirrorCS")])]});
            transform(context, id + "F10", {"entities" : qUnion([Q0]), "transformType" : TransformType.TRANSLATION_3D, "dx" : 0 * mm, "dy" : 0 * mm, "dz" : 0 * mm, "makeCopy" : true});
        }
    });
